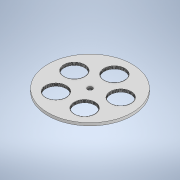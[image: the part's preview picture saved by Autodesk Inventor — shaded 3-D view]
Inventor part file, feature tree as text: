
AUTODESK INVENTOR PART (.ipt)
format: ipt  version: 2020.2 (Build 242310000, 310)  size: 2,896,896 bytes
history: native  units: in
note: dims shown in document units (in); Inventor stores cm internally (conversion verified against a paired STEP export)
features: sketch x12, thread x5, revolve x5, helix x5, extrude x1, hole x1
ambient origin geometry x8: Origin, YZ Plane, XZ Plane, XY Plane, X Axis, Y Axis, Z Axis, Center Point
bodies: Solid9 (feature_tree), Solid10 (feature_tree), Solid11 (feature_tree), Solid12 (feature_tree), Solid13 (feature_tree)
feature tree (29):
  extrude  "Extrusion2"  Depth=0.1in
  hole  "Hole1"  [1 undecoded]
  thread  "Thread3"  [1 undecoded]
  thread  "Thread4"  [1 undecoded]
  thread  "Thread5"  [1 undecoded]
  thread  "Thread6"  [1 undecoded]
  thread  "Thread7"  [1 undecoded]
  revolve  "Revolution7"  [1 undecoded]
  helix  "Coil7"  [1 undecoded]
  revolve  "Revolution8"  [1 undecoded]
  helix  "Coil8"  [1 undecoded]
  revolve  "Revolution9"  [1 undecoded]
  helix  "Coil9"  [1 undecoded]
  revolve  "Revolution10"  [1 undecoded]
  helix  "Coil10"  [1 undecoded]
  revolve  "Revolution11"  [1 undecoded]
  helix  "Coil11"  [1 undecoded]
  sketch  "Sketch1"  dims[d5=360.0deg d7=0.1in]
  sketch  "Sketch14"  dims[d8=0.0in d0=4.5274in d1=1.125in d2=1.3137in d17=0.3779in d28=1.9685in d30=360.0deg]
  sketch  "Sketch15"  dims[d32=0.15in d33=0.0in d36=0.15in d37=0.0in d38=0.2in d39=0.0in]
  sketch  "Sketch16"  dims[d40=0.2in d41=0.0in d42=0.2in d43=0.0in d44=0.2in d45=0.0in]
  sketch  "Sketch17"  dims[d53=0.3779in d71=0.3779in d89=0.3779in]
  sketch  "Sketch18"  dims[d107=0.3779in d125=0.3779in]
  sketch  "Sketch19"  dims[d136=0.266in d137=0.75in d138=0.507in d139=0.25in d140=0.5635in d141=1.0in d142=0.8108in d143=0.3779in d144=0.0038in d145=0.0038in]
  sketch  "Sketch20"  dims[d148=0.0236in d150=0.3779in d152=0.0in]
  sketch  "Sketch21"  dims[d153=0.0236in d154=0.1972in d155=0.3937in d156=0.0in d157=0.0in d158=0.0in d159=0.0in d160=0.0in]
  sketch  "Sketch22"  dims[d161=0.3779in d162=0.0038in d163=0.0038in]
  sketch  "Sketch23"  dims[d166=0.0236in]
  sketch  "Sketch24"  dims[d168=0.3779in d170=0.0in d171=0.0236in d172=0.1972in d173=0.3937in d174=0.0in d175=0.0in d176=0.0in d177=0.0in d178=0.0in d179=0.3779in d180=0.0038in d181=0.0038in d184=0.0236in d186=0.3779in d188=0.0in d189=0.0236in d190=0.1972in d191=0.3937in d192=0.0in d193=0.0in d194=0.0in d195=0.0in d196=0.0in d197=0.3779in d198=0.0038in d199=0.0038in d202=0.0236in d204=0.3779in d206=0.0in d207=0.0236in d208=0.1972in d209=0.3937in d210=0.0in d211=0.0in d212=0.0in d213=0.0in d214=0.0in d215=0.3779in d216=0.0038in d217=0.0038in d220=0.0236in d222=0.3779in d224=0.0in d225=0.0236in d226=0.1972in d227=0.3937in d228=0.0in d229=0.0in d230=0.0in d231=0.0in d232=0.0in]
note: 16 required parameter values undecoded (feature->parameter linkage not recoverable at this tier; creation-order binding heuristic only, values carry confidence <= 0.55)